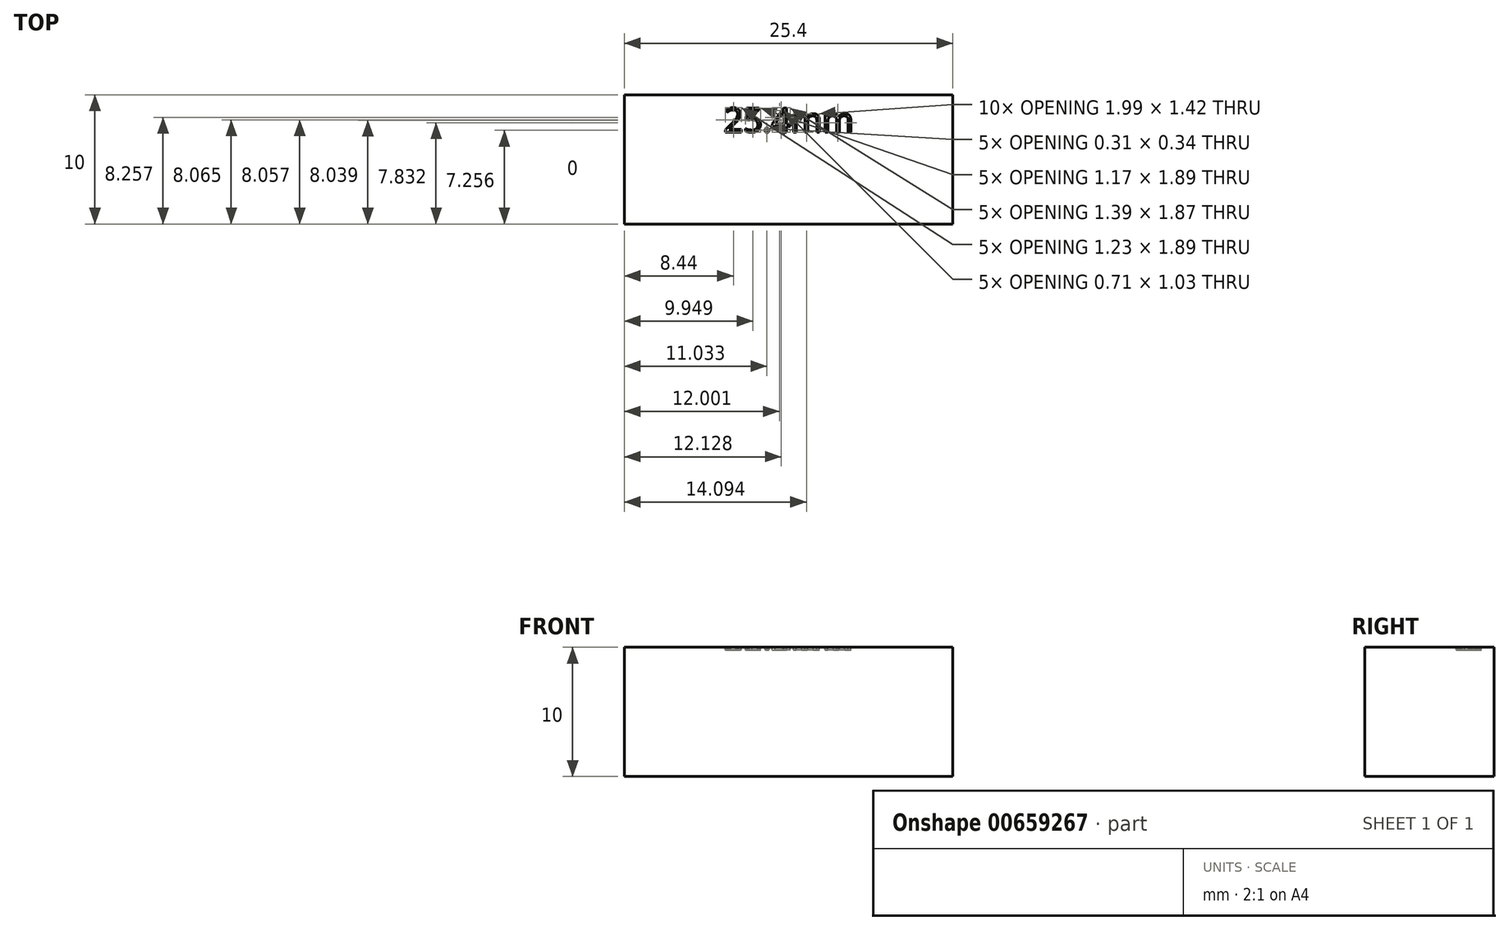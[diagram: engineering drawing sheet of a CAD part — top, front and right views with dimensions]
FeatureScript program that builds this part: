
annotation { "Feature Type Name" : "Feature", "Feature Type Description" : "" }
export const myFeature = defineFeature(function(context is Context, id is Id, definition is map)
    precondition{}
    {
        {
            var Q0;
            Q0=qCreatedBy(makeId("Top.planeOp"),FACE);
            var sketch = newSketch(context, id + "F0", { "sketchPlane" : qUnion([Q0])});
            skLineSegment(sketch, "E0.bottom", {"start": v(12.7, 5) * mm, "end": v(-12.7, 5) * mm});
            skLineSegment(sketch, "E0.top", {"start": v(12.7, -5) * mm, "end": v(-12.7, -5) * mm});
            skLineSegment(sketch, "E0.left", {"start": v(12.7, 5) * mm, "end": v(12.7, -5) * mm});
            skLineSegment(sketch, "E0.right", {"start": v(-12.7, 5) * mm, "end": v(-12.7, -5) * mm});
            skPoint(sketch, "E0.middle", {"position": v(0, 0) * mm});
            skSolve(sketch);
        }
        {
            var Q0;
            Q0 = qSketchRegion(id + "F0", true);
            extrude(context, id + "F1", {"entities" : qUnion([Q0]), "depth" : 10 * mm, "offsetDistance" : 25 * mm});
        }
        {
            var Q0;
            Q0=makeQuery(id+"F1.opExtrude","CAP_FACE",FACE,{"disambiguationData":[OSD([sQuery(id+"F0.wireOp",EDGE,"E0.bottom"),sQuery(id+"F0.wireOp",EDGE,"E0.top"),sQuery(id+"F0.wireOp",EDGE,"E0.left"),sQuery(id+"F0.wireOp",EDGE,"E0.right")])],"isStart":false});
            var sketch = newSketch(context, id + "F2", { "sketchPlane" : qUnion([Q0])});
            skText(sketch, "E1", { "text": "25.4mm", "fontName": "OpenSans-Regular.ttf"});
            skLineSegment(sketch, "E2", {"start": v(0, 0) * mm, "end": v(0, 2.12) * mm, "construction": true});
            const initialGuessF2  = {"E1": [-0.005, 0.00212, 1, 0, 0.00188]};
            skSetInitialGuess(sketch, initialGuessF2);
            skSolve(sketch);
        }
        {
            var Q0;
            Q0 = qSketchRegion(id + "F2", true);
            extrude(context, id + "F3", {"entities" : qUnion([Q0]), "operationType" : NewBodyOperationType.REMOVE, "oppositeDirection" : true, "depth" : .2 * mm, "offsetDistance" : 25 * mm});
        }
    });
